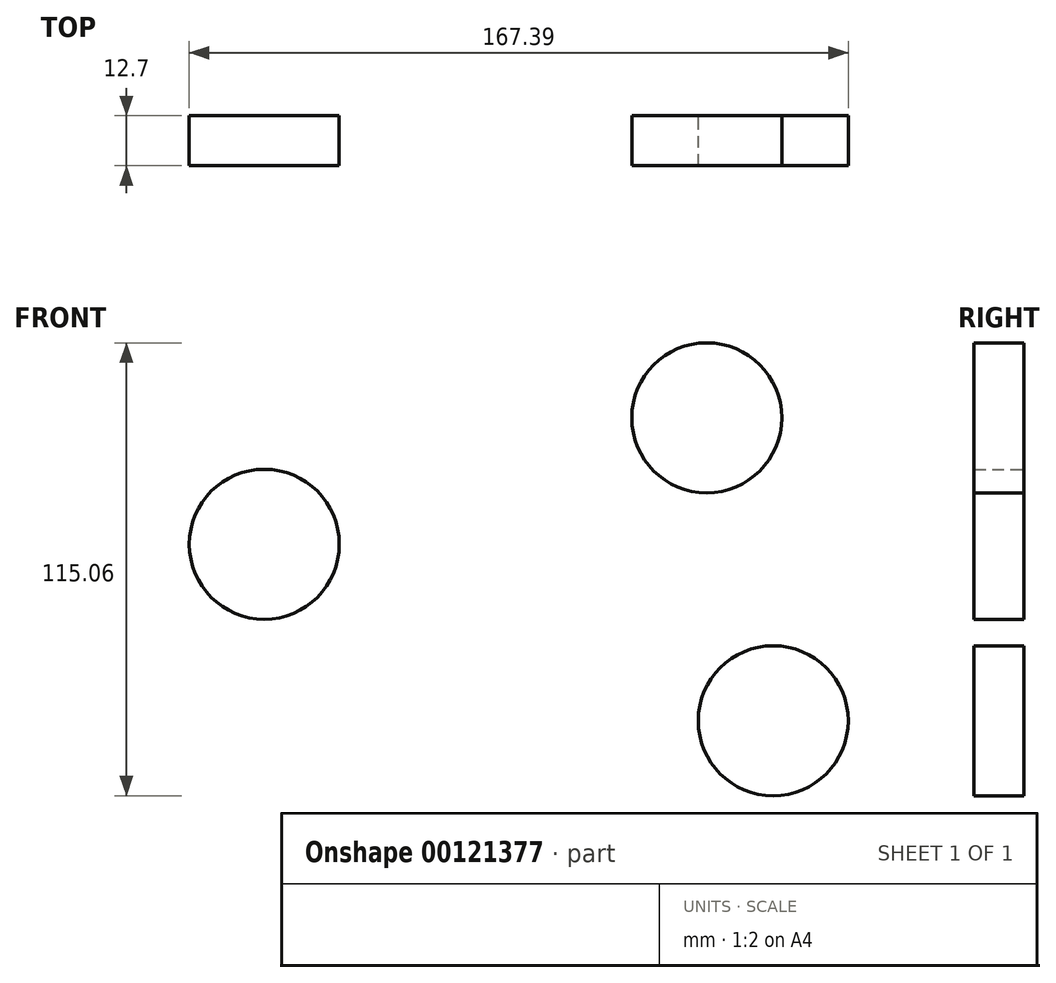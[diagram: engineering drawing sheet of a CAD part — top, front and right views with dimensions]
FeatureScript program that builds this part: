
annotation { "Feature Type Name" : "Feature", "Feature Type Description" : "" }
export const myFeature = defineFeature(function(context is Context, id is Id, definition is map)
    precondition{}
    {
        {
            var Q0;
            Q0=qCreatedBy(makeId("Front.planeOp"),FACE);
            var sketch = newSketch(context, id + "F0", { "sketchPlane" : qUnion([Q0])});
            skCircle(sketch, "E0", {"center": v(41.8, 55.37) * mm, "radius": 19.05 * mm});
            skCircle(sketch, "E1", {"center": v(58.7, -21.6) * mm, "radius": 19.05 * mm});
            skCircle(sketch, "E2", {"center": v(-70.6, 23.26) * mm, "radius": 19.05 * mm});
            skArc(sketch, "E3", {"start": v(-70.6, 23.26) * mm, "mid": v(-12.77, 33.61) * mm, "end": v(41.8, 55.37) * mm});
            skArc(sketch, "E4", {"start": v(58.7, -21.6) * mm, "mid": v(-3.07, 9.13) * mm, "end": v(-70.6, 23.26) * mm});
            skArc(sketch, "E5", {"start": v(41.8, 55.37) * mm, "mid": v(42.6, 15.21) * mm, "end": v(58.7, -21.6) * mm});
            skSolve(sketch);
        }
        {
            var Q0;
            {var subQ0=sQuery(id+"F0.wireOp",EDGE,"E3");var subQ1=sQuery(id+"F0.wireOp",EDGE,"E0");var subQ2=makeQuery(id+"F0.imprint","INTERSECT",VERTEX,{"derivedFrom":[subQ1,subQ0]});Q0=makeQuery(id+"F0.imprint","IMPRINT",FACE,{"disambiguationData":[TD([[makeQuery(id+"F0.imprint","IMPRINT",EDGE,{"disambiguationData":[TD([[subQ2,1.0]])],"derivedFrom":subQ1}),1.0]])]});}
            var Q1;
            {var subQ0=sQuery(id+"F0.wireOp",EDGE,"E4");var subQ1=sQuery(id+"F0.wireOp",EDGE,"E1");var subQ2=makeQuery(id+"F0.imprint","INTERSECT",VERTEX,{"derivedFrom":[subQ1,subQ0]});Q1=makeQuery(id+"F0.imprint","IMPRINT",FACE,{"disambiguationData":[TD([[makeQuery(id+"F0.imprint","IMPRINT",EDGE,{"disambiguationData":[TD([[subQ2,-1.0]])],"derivedFrom":subQ1}),1.0]])]});}
            var Q2;
            {var subQ0=sQuery(id+"F0.wireOp",EDGE,"E3");var subQ1=sQuery(id+"F0.wireOp",EDGE,"E2");var subQ2=makeQuery(id+"F0.imprint","INTERSECT",VERTEX,{"derivedFrom":[subQ1,subQ0]});Q2=makeQuery(id+"F0.imprint","IMPRINT",FACE,{"disambiguationData":[TD([[makeQuery(id+"F0.imprint","IMPRINT",EDGE,{"disambiguationData":[TD([[subQ2,-1.0]])],"derivedFrom":subQ1}),1.0]])]});}
            var Q3;
            {var subQ0=sQuery(id+"F0.wireOp",EDGE,"E3");var subQ1=sQuery(id+"F0.wireOp",EDGE,"E0");var subQ2=makeQuery(id+"F0.imprint","INTERSECT",VERTEX,{"derivedFrom":[subQ1,subQ0]});Q3=makeQuery(id+"F0.imprint","IMPRINT",FACE,{"disambiguationData":[TD([[makeQuery(id+"F0.imprint","IMPRINT",EDGE,{"disambiguationData":[TD([[subQ2,-1.0]])],"derivedFrom":subQ1}),1.0]])]});}
            var Q4;
            {var subQ0=sQuery(id+"F0.wireOp",EDGE,"E4");var subQ1=sQuery(id+"F0.wireOp",EDGE,"E1");var subQ2=makeQuery(id+"F0.imprint","INTERSECT",VERTEX,{"derivedFrom":[subQ1,subQ0]});Q4=makeQuery(id+"F0.imprint","IMPRINT",FACE,{"disambiguationData":[TD([[makeQuery(id+"F0.imprint","IMPRINT",EDGE,{"disambiguationData":[TD([[subQ2,1.0]])],"derivedFrom":subQ1}),1.0]])]});}
            var Q5;
            {var subQ0=sQuery(id+"F0.wireOp",EDGE,"E3");var subQ1=sQuery(id+"F0.wireOp",EDGE,"E2");var subQ2=makeQuery(id+"F0.imprint","INTERSECT",VERTEX,{"derivedFrom":[subQ1,subQ0]});Q5=makeQuery(id+"F0.imprint","IMPRINT",FACE,{"disambiguationData":[TD([[makeQuery(id+"F0.imprint","IMPRINT",EDGE,{"disambiguationData":[TD([[subQ2,1.0]])],"derivedFrom":subQ1}),1.0]])]});}
            extrude(context, id + "F1", {"entities" : qUnion([Q0, Q1, Q2, Q3, Q4, Q5]), "endBound" : BoundingType.SYMMETRIC, "depth" : 12.7 * mm});
        }
    });
